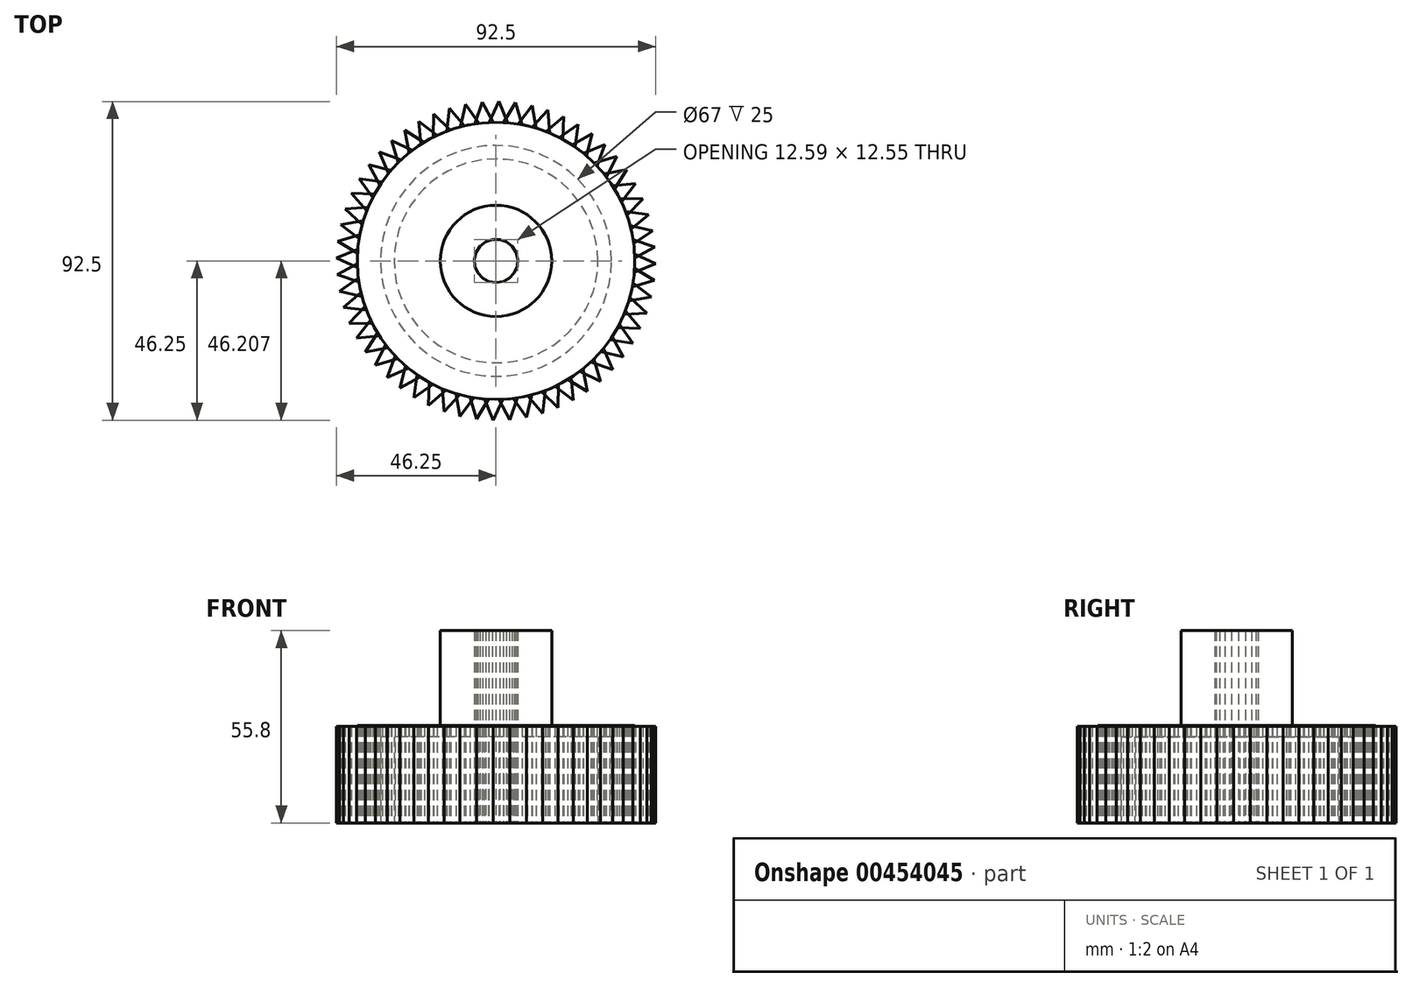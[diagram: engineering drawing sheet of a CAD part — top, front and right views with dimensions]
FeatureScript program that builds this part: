
annotation { "Feature Type Name" : "Feature", "Feature Type Description" : "" }
export const myFeature = defineFeature(function(context is Context, id is Id, definition is map)
    precondition{}
    {
        {
            var Q0;
            Q0=qCreatedBy(makeId("Front.planeOp"),FACE);
            var sketch = newSketch(context, id + "F0", { "sketchPlane" : qUnion([Q0])});
            skLineSegment(sketch, "E0.bottom", {"start": v(0, 0) * mm, "end": v(-40.22, 0) * mm});
            skLineSegment(sketch, "E0.top", {"start": v(0, 55.8) * mm, "end": v(-40.22, 55.8) * mm});
            skLineSegment(sketch, "E0.left", {"start": v(0, 0) * mm, "end": v(0, 55.8) * mm});
            skLineSegment(sketch, "E0.right", {"start": v(-40.22, 0) * mm, "end": v(-40.22, 55.8) * mm});
            skSolve(sketch);
        }
        {
            var Q0;
            Q0=makeQuery(id+"F0.imprint","IMPRINT",FACE,{"disambiguationData":[TD([[makeQuery(id+"F0.imprint","IMPRINT",EDGE,{"derivedFrom":sQuery(id+"F0.wireOp",EDGE,"E0.bottom")}),-1.0]])]});
            var Q1;
            Q1=sQuery(id+"F0.wireOp",EDGE,"E0.left");
            revolve(context, id + "F1", {"entities" : qUnion([Q0]), "axis" : qUnion([Q1]), "revolveType" : RevolveType.FULL});
        }
        {
            var Q0;
            Q0=qCreatedBy(makeId("Front.planeOp"),FACE);
            var sketch = newSketch(context, id + "F2", { "sketchPlane" : qUnion([Q0])});
            skLineSegment(sketch, "E1.bottom", {"start": v(-40.8, 56.37) * mm, "end": v(-16.15, 56.37) * mm});
            skLineSegment(sketch, "E1.top", {"start": v(-40.8, 28.33) * mm, "end": v(-16.15, 28.33) * mm});
            skLineSegment(sketch, "E1.left", {"start": v(-40.8, 56.37) * mm, "end": v(-40.8, 28.33) * mm});
            skLineSegment(sketch, "E1.right", {"start": v(-16.15, 56.37) * mm, "end": v(-16.15, 28.33) * mm});
            skLineSegment(sketch, "E2", {"start": v(0, 55.8) * mm, "end": v(0, 0) * mm});
            skSolve(sketch);
        }
        {
            var Q0;
            Q0 = qSketchRegion(id + "F2", true);
            var Q1;
            Q1=sQuery(id+"F2.wireOp",EDGE,"E2");
            revolve(context, id + "F3", {"operationType" : NewBodyOperationType.REMOVE, "entities" : qUnion([Q0]), "axis" : qUnion([Q1]), "revolveType" : RevolveType.FULL, "oppositeDirection" : true});
        }
        {
            var Q0;
            Q0=qCreatedBy(makeId("Top.planeOp"),FACE);
            var sketch = newSketch(context, id + "F4", { "sketchPlane" : qUnion([Q0])});
            skCircle(sketch, "E3", {"center": v(0, 0) * mm, "radius": 33.5 * mm});
            skCircle(sketch, "E4", {"center": v(0, 0) * mm, "radius": 29.56 * mm});
            skSolve(sketch);
        }
        {
            var Q0;
            Q0 = qSketchRegion(id + "F4", true);
            extrude(context, id + "F5", {"entities" : qUnion([Q0]), "operationType" : NewBodyOperationType.REMOVE, "depth" : 25 * mm});
        }
        {
            var Q0;
            Q0=qCreatedBy(makeId("Top.planeOp"),FACE);
            var sketch = newSketch(context, id + "F6", { "sketchPlane" : qUnion([Q0])});
            skCircle(sketch, "E5.cCircle", {"center": v(0, 0) * mm, "radius": 6.23 * mm, "construction": true});
            skLineSegment(sketch, "E5.0", {"start": v(-1.04, 6.23) * mm, "end": v(1.04, 6.23) * mm});
            skLineSegment(sketch, "E5.1", {"start": v(1.04, 6.23) * mm, "end": v(3, 5.56) * mm});
            skLineSegment(sketch, "E5.2", {"start": v(3, 5.56) * mm, "end": v(4.65, 4.28) * mm});
            skLineSegment(sketch, "E5.3", {"start": v(4.65, 4.28) * mm, "end": v(5.79, 2.54) * mm});
            skLineSegment(sketch, "E5.4", {"start": v(5.79, 2.54) * mm, "end": v(6.3, 0.52) * mm});
            skLineSegment(sketch, "E5.5", {"start": v(6.3, 0.52) * mm, "end": v(6.12, -1.55) * mm});
            skLineSegment(sketch, "E5.6", {"start": v(6.12, -1.55) * mm, "end": v(5.29, -3.46) * mm});
            skLineSegment(sketch, "E5.7", {"start": v(5.29, -3.46) * mm, "end": v(3.88, -4.99) * mm});
            skLineSegment(sketch, "E5.8", {"start": v(3.88, -4.99) * mm, "end": v(2.05, -5.98) * mm});
            skLineSegment(sketch, "E5.9", {"start": v(2.05, -5.98) * mm, "end": v(0, -6.32) * mm});
            skLineSegment(sketch, "E5.10", {"start": v(0, -6.32) * mm, "end": v(-2.05, -5.98) * mm});
            skLineSegment(sketch, "E5.11", {"start": v(-2.05, -5.98) * mm, "end": v(-3.88, -4.99) * mm});
            skLineSegment(sketch, "E5.12", {"start": v(-3.88, -4.99) * mm, "end": v(-5.29, -3.46) * mm});
            skLineSegment(sketch, "E5.13", {"start": v(-5.29, -3.46) * mm, "end": v(-6.12, -1.55) * mm});
            skLineSegment(sketch, "E5.14", {"start": v(-6.12, -1.55) * mm, "end": v(-6.3, 0.52) * mm});
            skLineSegment(sketch, "E5.15", {"start": v(-6.3, 0.52) * mm, "end": v(-5.79, 2.54) * mm});
            skLineSegment(sketch, "E5.16", {"start": v(-5.79, 2.54) * mm, "end": v(-4.65, 4.28) * mm});
            skLineSegment(sketch, "E5.17", {"start": v(-4.65, 4.28) * mm, "end": v(-3, 5.56) * mm});
            skLineSegment(sketch, "E5.18", {"start": v(-3, 5.56) * mm, "end": v(-1.04, 6.23) * mm});
            skPoint(sketch, "E5.0.midPoint", {"position": v(0, 6.23) * mm});
            skSolve(sketch);
        }
        {
            var Q0;
            Q0=makeQuery(id+"F6.imprint","IMPRINT",FACE,{"disambiguationData":[TD([[makeQuery(id+"F6.imprint","IMPRINT",EDGE,{"derivedFrom":sQuery(id+"F6.wireOp",EDGE,"E5.0")}),-1.0]])]});
            extrude(context, id + "F7", {"entities" : qUnion([Q0]), "operationType" : NewBodyOperationType.REMOVE, "depth" : 60 * mm});
        }
        {
            var Q0;
            Q0=qCreatedBy(makeId("Top.planeOp"),FACE);
            var sketch = newSketch(context, id + "F8", { "sketchPlane" : qUnion([Q0])});
            skLineSegment(sketch, "E6", {"start": v(2.17, 40.08) * mm, "end": v(5.68, 45.91) * mm});
            skLineSegment(sketch, "E7", {"start": v(5.68, 45.91) * mm, "end": v(7.56, 39.44) * mm});
            skLineSegment(sketch, "E8", {"start": v(2.17, 40.08) * mm, "end": v(7.56, 39.44) * mm});
            skSolve(sketch);
        }
        {
            var Q0;
            Q0=makeQuery(id+"F8.imprint","IMPRINT",FACE,{"disambiguationData":[TD([[makeQuery(id+"F8.imprint","IMPRINT",EDGE,{"derivedFrom":sQuery(id+"F8.wireOp",EDGE,"E6")}),-1.0]])]});
            extrude(context, id + "F9", {"entities" : qUnion([Q0]), "depth" : 28 * mm});
        }
        {
            var Q0;
            Q0=makeQuery(id+"F9.opExtrude","SWEPT_BODY",BODY,{"disambiguationData":[OSD([sQuery(id+"F8.wireOp",EDGE,"E6"),sQuery(id+"F8.wireOp",EDGE,"E7"),sQuery(id+"F8.wireOp",EDGE,"E8")])]});
            var Q1;
            Q1=makeQuery(id+"F1.opRevolve","SWEPT_FACE",FACE,{"disambiguationData":[OSD([sQuery(id+"F0.wireOp",EDGE,"E0.right")])]});
            circularPattern(context, id + "F10", {"entities" : qUnion([Q0]), "axis" : qUnion([Q1]), "angle" : 360 * degree, "instanceCount" : 60, "equalSpace" : true});
        }
    });
